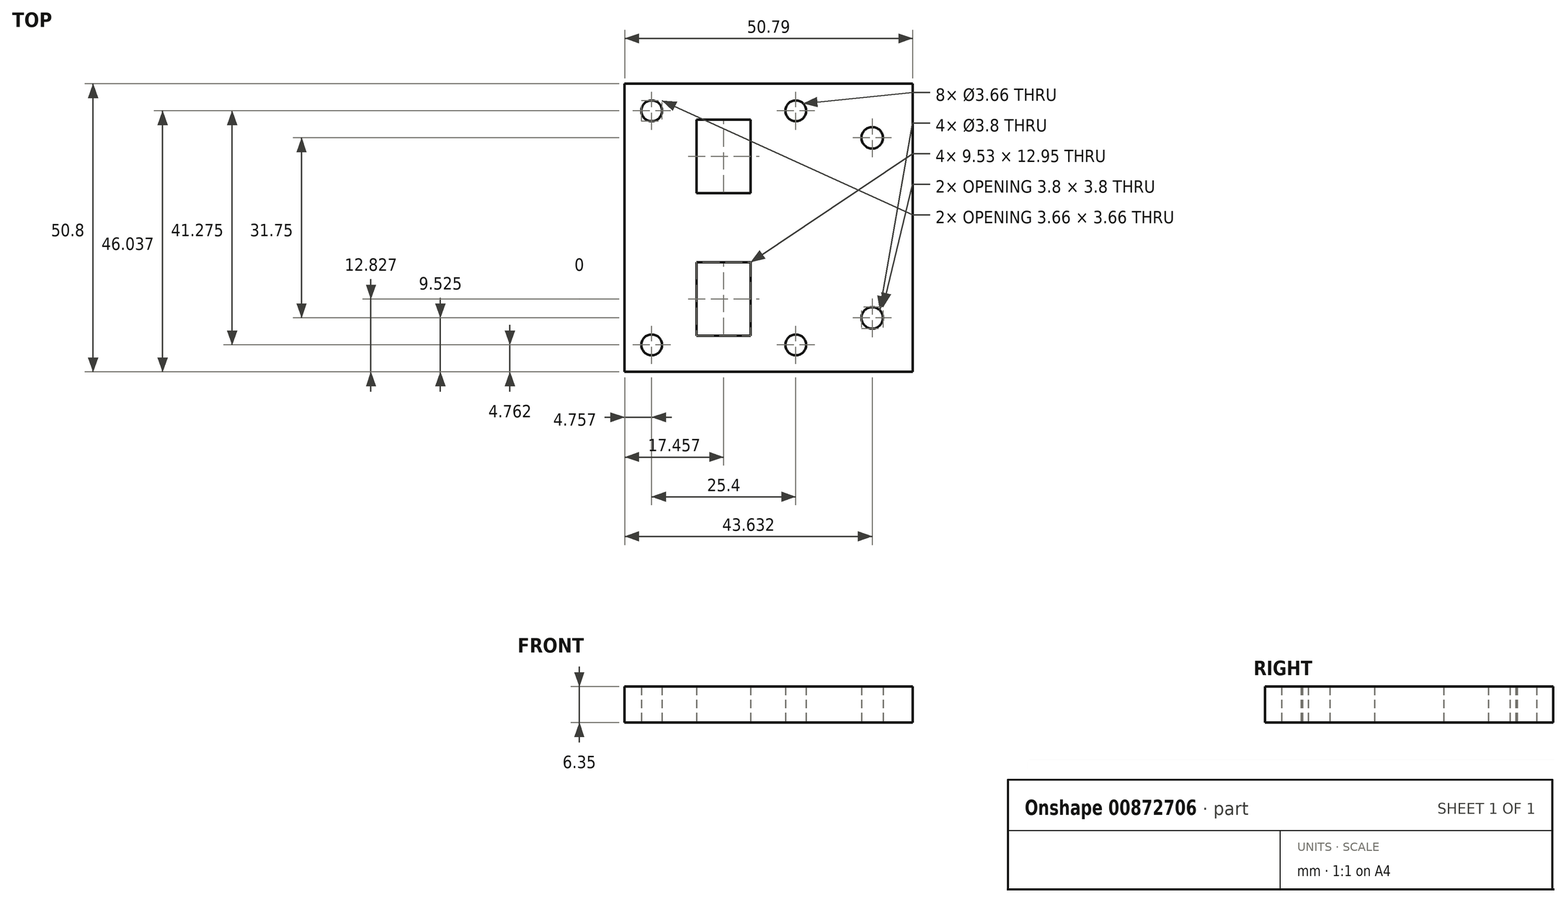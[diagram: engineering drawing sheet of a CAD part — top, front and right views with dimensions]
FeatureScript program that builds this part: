
annotation { "Feature Type Name" : "Feature", "Feature Type Description" : "" }
export const myFeature = defineFeature(function(context is Context, id is Id, definition is map)
    precondition{}
    {
        {
            var Q0;
            Q0=qCreatedBy(makeId("Top.planeOp"),FACE);
            var sketch = newSketch(context, id + "F0", { "sketchPlane" : qUnion([Q0])});
            skLineSegment(sketch, "E0.bottom", {"start": v(-152.4, 152.4) * mm, "end": v(152.4, 152.4) * mm});
            skLineSegment(sketch, "E0.top", {"start": v(-152.4, -152.4) * mm, "end": v(152.4, -152.4) * mm});
            skLineSegment(sketch, "E0.left", {"start": v(-152.4, 152.4) * mm, "end": v(-152.4, -152.4) * mm});
            skLineSegment(sketch, "E0.right", {"start": v(152.4, 152.4) * mm, "end": v(152.4, -152.4) * mm});
            skPoint(sketch, "E0.middle", {"position": v(0, 0) * mm});
            skLineSegment(sketch, "E1.0", {"start": v(-107.95, -82.55) * mm, "end": v(107.95, -82.55) * mm});
            skLineSegment(sketch, "E2.0", {"start": v(-107.95, 107.95) * mm, "end": v(-107.95, -82.55) * mm});
            skLineSegment(sketch, "E3", {"start": v(0, 152.4) * mm, "end": v(0, -152.4) * mm, "construction": true});
            skLineSegment(sketch, "E4", {"start": v(-152.4, 0) * mm, "end": v(152.4, 0) * mm, "construction": true});
            skLineSegment(sketch, "E5.MirrorCS", {"start": v(107.95, 107.95) * mm, "end": v(107.95, -82.55) * mm});
            skLineSegment(sketch, "E6.0", {"start": v(-107.95, 107.95) * mm, "end": v(107.95, 107.95) * mm});
            skLineSegment(sketch, "E7.bottom", {"start": v(-104.78, 25.4) * mm, "end": v(-53.98, 25.4) * mm});
            skLineSegment(sketch, "E7.top", {"start": v(-104.78, -25.4) * mm, "end": v(-53.98, -25.4) * mm});
            skLineSegment(sketch, "E7.left", {"start": v(-104.78, 25.4) * mm, "end": v(-104.78, -25.4) * mm});
            skLineSegment(sketch, "E7.right", {"start": v(-69.85, 25.4) * mm, "end": v(-69.85, -25.4) * mm});
            skLineSegment(sketch, "E8", {"start": v(-87.31, 25.4) * mm, "end": v(-87.31, -152.4) * mm, "construction": true});
            skLineSegment(sketch, "E9.bottom", {"start": v(-82.55, 6.1) * mm, "end": v(-92.08, 6.1) * mm});
            skLineSegment(sketch, "E9.top", {"start": v(-82.55, 19.05) * mm, "end": v(-92.08, 19.05) * mm});
            skLineSegment(sketch, "E9.left", {"start": v(-82.55, 6.1) * mm, "end": v(-82.55, 19.05) * mm});
            skLineSegment(sketch, "E9.right", {"start": v(-92.08, 6.1) * mm, "end": v(-92.08, 19.05) * mm});
            skPoint(sketch, "E9.middle", {"position": v(-87.31, 12.57) * mm});
            skPoint(sketch, "E10", {"position": v(-69.85, 0) * mm});
            skLineSegment(sketch, "E11.MirrorCS", {"start": v(-92.08, -6.1) * mm, "end": v(-92.08, -19.05) * mm});
            skLineSegment(sketch, "E12.MirrorCS", {"start": v(-82.55, -6.1) * mm, "end": v(-82.55, -19.05) * mm});
            skPoint(sketch, "E13.MirrorP", {"position": v(-87.31, -12.57) * mm});
            skLineSegment(sketch, "E14.MirrorCS", {"start": v(-82.55, -6.1) * mm, "end": v(-92.08, -6.1) * mm});
            skLineSegment(sketch, "E15.MirrorCS", {"start": v(-82.55, -19.05) * mm, "end": v(-92.08, -19.05) * mm});
            skCircle(sketch, "E16", {"center": v(-101.6, -127) * mm, "radius": 11.43 * mm});
            skCircle(sketch, "E17", {"center": v(-86.1, -111.5) * mm, "radius": 1.59 * mm});
            skCircle(sketch, "E18.1.0", {"center": v(-117.1, -111.5) * mm, "radius": 1.59 * mm});
            skCircle(sketch, "E18.2.0", {"center": v(-117.1, -142.5) * mm, "radius": 1.59 * mm});
            skCircle(sketch, "E18.3.0", {"center": v(-86.1, -142.5) * mm, "radius": 1.59 * mm});
            skCircle(sketch, "E19.MirrorC", {"center": v(117.1, -111.5) * mm, "radius": 1.59 * mm});
            skCircle(sketch, "E20.MirrorC", {"center": v(86.1, -111.5) * mm, "radius": 1.59 * mm});
            skCircle(sketch, "E21.MirrorC", {"center": v(117.1, -142.5) * mm, "radius": 1.59 * mm});
            skPoint(sketch, "E22.MirrorP", {"position": v(101.6, -127) * mm});
            skCircle(sketch, "E23.MirrorC", {"center": v(86.1, -142.5) * mm, "radius": 1.59 * mm});
            skCircle(sketch, "E24.MirrorC", {"center": v(101.6, -127) * mm, "radius": 11.43 * mm});
            skPoint(sketch, "E25.orphan", {"position": v(-87.31, -25.4) * mm});
            skCircle(sketch, "E26", {"center": v(-103.19, -89.7) * mm, "radius": 1.59 * mm});
            skCircle(sketch, "E27.MirrorC", {"center": v(-71.44, -89.7) * mm, "radius": 1.59 * mm});
            skLineSegment(sketch, "E28.bottom", {"start": v(-96.84, -82.55) * mm, "end": v(-77.79, -82.55) * mm});
            skLineSegment(sketch, "E28.top", {"start": v(-96.84, -96.85) * mm, "end": v(-77.79, -96.85) * mm});
            skLineSegment(sketch, "E28.left", {"start": v(-96.84, -82.55) * mm, "end": v(-96.84, -96.85) * mm});
            skLineSegment(sketch, "E28.right", {"start": v(-77.79, -82.55) * mm, "end": v(-77.79, -96.85) * mm});
            skPoint(sketch, "E29", {"position": v(-87.31, -96.85) * mm});
            skLineSegment(sketch, "E30.MirrorCS", {"start": v(96.84, -82.55) * mm, "end": v(96.84, -96.85) * mm});
            skCircle(sketch, "E31.MirrorC", {"center": v(71.44, -89.7) * mm, "radius": 1.59 * mm});
            skCircle(sketch, "E32.MirrorC", {"center": v(103.19, -89.7) * mm, "radius": 1.59 * mm});
            skLineSegment(sketch, "E33.MirrorCS", {"start": v(96.84, -82.55) * mm, "end": v(77.79, -82.55) * mm});
            skPoint(sketch, "E34.MirrorP", {"position": v(87.31, -96.85) * mm});
            skLineSegment(sketch, "E35.MirrorCS", {"start": v(77.79, -82.55) * mm, "end": v(77.79, -96.85) * mm});
            skLineSegment(sketch, "E36.MirrorCS", {"start": v(96.84, -96.85) * mm, "end": v(77.79, -96.85) * mm});
            skLineSegment(sketch, "E37", {"start": v(107.95, 12.7) * mm, "end": v(-107.95, 12.57) * mm, "construction": true});
            skCircle(sketch, "E38.MirrorC", {"center": v(-103.3, 114.85) * mm, "radius": 1.59 * mm});
            skLineSegment(sketch, "E39.MirrorCS", {"start": v(-96.97, 122) * mm, "end": v(-77.92, 122.03) * mm});
            skLineSegment(sketch, "E40.MirrorCS", {"start": v(-96.95, 107.7) * mm, "end": v(-77.9, 107.73) * mm});
            skCircle(sketch, "E41.MirrorC", {"center": v(103.07, 115.1) * mm, "radius": 1.59 * mm});
            skLineSegment(sketch, "E42.MirrorCS", {"start": v(-96.95, 107.7) * mm, "end": v(-96.97, 122) * mm});
            skCircle(sketch, "E43.MirrorC", {"center": v(-71.56, 114.89) * mm, "radius": 1.59 * mm});
            skLineSegment(sketch, "E44.MirrorCS", {"start": v(96.7, 122.24) * mm, "end": v(77.66, 122.21) * mm});
            skCircle(sketch, "E45.MirrorC", {"center": v(71.32, 115.06) * mm, "radius": 1.59 * mm});
            skLineSegment(sketch, "E46.MirrorCS", {"start": v(96.73, 107.94) * mm, "end": v(77.68, 107.91) * mm});
            skPoint(sketch, "E47.MirrorP", {"position": v(-87.44, 122.02) * mm});
            skPoint(sketch, "E48.MirrorP", {"position": v(87.18, 122.23) * mm});
            skLineSegment(sketch, "E49.MirrorCS", {"start": v(-108.06, 107.7) * mm, "end": v(107.84, 107.95) * mm});
            skLineSegment(sketch, "E50.MirrorCS", {"start": v(77.68, 107.91) * mm, "end": v(77.66, 122.21) * mm});
            skLineSegment(sketch, "E51.MirrorCS", {"start": v(-77.9, 107.73) * mm, "end": v(-77.92, 122.03) * mm});
            skLineSegment(sketch, "E52.MirrorCS", {"start": v(96.73, 107.94) * mm, "end": v(96.7, 122.24) * mm});
            skLineSegment(sketch, "E53.0", {"start": v(-53.98, 25.4) * mm, "end": v(-53.98, -25.4) * mm});
            skCircle(sketch, "E54", {"center": v(-61.14, 15.87) * mm, "radius": 1.59 * mm});
            skCircle(sketch, "E55.MirrorC", {"center": v(-61.14, -15.88) * mm, "radius": 1.59 * mm});
            skCircle(sketch, "E56", {"center": v(-100.01, 20.64) * mm, "radius": 1.83 * mm});
            skCircle(sketch, "E57.MirrorC", {"center": v(-100.01, -20.64) * mm, "radius": 1.83 * mm});
            skCircle(sketch, "E58.MirrorC", {"center": v(-74.61, 20.64) * mm, "radius": 1.83 * mm});
            skCircle(sketch, "E59.MirrorC", {"center": v(-74.61, -20.64) * mm, "radius": 1.83 * mm});
            skSolve(sketch);
        }
        {
            var Q0;
            {var subQ1=sQuery(id+"F0.wireOp",EDGE,"E7.right");Q0=makeQuery(id+"F0.imprint","IMPRINT",FACE,{"disambiguationData":[TD([[makeQuery(id+"F0.imprint","IMPRINT",EDGE,{"derivedFrom":subQ1}),1.0]])]});}
            var Q1;
            {var subQ0=sQuery(id+"F0.wireOp",EDGE,"E7.left");Q1=makeQuery(id+"F0.imprint","IMPRINT",FACE,{"disambiguationData":[TD([[makeQuery(id+"F0.imprint","IMPRINT",EDGE,{"derivedFrom":subQ0}),1.0]])]});}
            var Q2;
            Q2=makeQuery(id+"F0.imprint","IMPRINT",FACE,{"disambiguationData":[TD([[makeQuery(id+"F0.imprint","IMPRINT",EDGE,{"derivedFrom":sQuery(id+"F0.wireOp",EDGE,"E57.MirrorC")}),-1.0]])]});
            var Q3;
            Q3=makeQuery(id+"F0.imprint","IMPRINT",FACE,{"disambiguationData":[TD([[makeQuery(id+"F0.imprint","IMPRINT",EDGE,{"derivedFrom":sQuery(id+"F0.wireOp",EDGE,"E56")}),1.0]])]});
            var Q4;
            Q4=makeQuery(id+"F0.imprint","IMPRINT",FACE,{"disambiguationData":[TD([[makeQuery(id+"F0.imprint","IMPRINT",EDGE,{"derivedFrom":sQuery(id+"F0.wireOp",EDGE,"E58.MirrorC")}),-1.0]])]});
            var Q5;
            Q5=makeQuery(id+"F0.imprint","IMPRINT",FACE,{"disambiguationData":[TD([[makeQuery(id+"F0.imprint","IMPRINT",EDGE,{"derivedFrom":sQuery(id+"F0.wireOp",EDGE,"E59.MirrorC")}),1.0]])]});
            var Q6;
            Q6=makeQuery(id+"F0.imprint","IMPRINT",FACE,{"disambiguationData":[TD([[makeQuery(id+"F0.imprint","IMPRINT",EDGE,{"derivedFrom":sQuery(id+"F0.wireOp",EDGE,"E54")}),1.0]])]});
            var Q7;
            Q7=makeQuery(id+"F0.imprint","IMPRINT",FACE,{"disambiguationData":[TD([[makeQuery(id+"F0.imprint","IMPRINT",EDGE,{"derivedFrom":sQuery(id+"F0.wireOp",EDGE,"E55.MirrorC")}),-1.0]])]});
            var Q8;
            {var subQ3=sQuery(id+"F0.wireOp",EDGE,"E7.right");Q8=makeQuery(id+"F0.imprint","IMPRINT",FACE,{"disambiguationData":[TD([[makeQuery(id+"F0.imprint","IMPRINT",EDGE,{"derivedFrom":subQ3}),-1.0]])]});}
            extrude(context, id + "F1", {"entities" : qUnion([Q0, Q1, Q2, Q3, Q4, Q5, Q6, Q7, Q8]), "depth" : 6.35 * mm, "offsetDistance" : 25.4 * mm});
        }
        {
            var Q0;
            Q0=sQuery(id+"F0.wireOp",VERTEX,"E56.center");
            var Q1;
            Q1=sQuery(id+"F0.wireOp",VERTEX,"E58.MirrorC.center");
            var Q2;
            Q2=sQuery(id+"F0.wireOp",VERTEX,"E59.MirrorC.center");
            var Q3;
            Q3=sQuery(id+"F0.wireOp",VERTEX,"E57.MirrorC.center");
            var Q4;
            Q4=makeQuery(id+"F1.opExtrude","SWEPT_BODY",BODY,{"disambiguationData":[OSD([sQuery(id+"F0.wireOp",EDGE,"E7.bottom"),sQuery(id+"F0.wireOp",EDGE,"E7.top"),sQuery(id+"F0.wireOp",EDGE,"E7.left"),sQuery(id+"F0.wireOp",EDGE,"E9.bottom"),sQuery(id+"F0.wireOp",EDGE,"E9.top"),sQuery(id+"F0.wireOp",EDGE,"E9.left"),sQuery(id+"F0.wireOp",EDGE,"E9.right"),sQuery(id+"F0.wireOp",EDGE,"E11.MirrorCS"),sQuery(id+"F0.wireOp",EDGE,"E12.MirrorCS"),sQuery(id+"F0.wireOp",EDGE,"E14.MirrorCS"),sQuery(id+"F0.wireOp",EDGE,"E15.MirrorCS"),sQuery(id+"F0.wireOp",EDGE,"E53.0")])]});
            hole(context, id + "F2", {"style" : HoleStyle.SIMPLE, "endStyle" : HoleEndStyle.THROUGH, "oppositeDirection" : true, "standardTappedOrClearance" : lookupTablePath({ "fit" : "Close", "standard" : "ANSI", "size" : "#6", "type" : "Clearance" }), "standardBlindInLast" : lookupTablePath({ "fit" : "Close", "standard" : "ANSI", "size" : "#6", "type" : "Clearance" }), "holeDiameter" : 3.66 * mm, "majorDiameter" : 6.35 * mm, "isTappedThrough" : true, "tappedDepth" : 12.7 * mm, "tapClearance" : 3, "locations" : qUnion([Q0, Q1, Q2, Q3]), "scope" : qUnion([Q4])});
        }
        {
            var Q0;
            Q0=sQuery(id+"F0.wireOp",VERTEX,"E55.MirrorC.center");
            var Q1;
            Q1=sQuery(id+"F0.wireOp",VERTEX,"E54.center");
            var Q2;
            Q2=makeQuery(id+"F1.opExtrude","SWEPT_BODY",BODY,{"disambiguationData":[OSD([sQuery(id+"F0.wireOp",EDGE,"E7.bottom"),sQuery(id+"F0.wireOp",EDGE,"E7.top"),sQuery(id+"F0.wireOp",EDGE,"E7.left"),sQuery(id+"F0.wireOp",EDGE,"E9.bottom"),sQuery(id+"F0.wireOp",EDGE,"E9.top"),sQuery(id+"F0.wireOp",EDGE,"E9.left"),sQuery(id+"F0.wireOp",EDGE,"E9.right"),sQuery(id+"F0.wireOp",EDGE,"E11.MirrorCS"),sQuery(id+"F0.wireOp",EDGE,"E12.MirrorCS"),sQuery(id+"F0.wireOp",EDGE,"E14.MirrorCS"),sQuery(id+"F0.wireOp",EDGE,"E15.MirrorCS"),sQuery(id+"F0.wireOp",EDGE,"E53.0")])]});
            hole(context, id + "F3", {"style" : HoleStyle.SIMPLE, "endStyle" : HoleEndStyle.THROUGH, "oppositeDirection" : true, "standardTappedOrClearance" : lookupTablePath({ "fit" : "Normal (ASME)", "standard" : "ANSI", "size" : "#6", "type" : "Clearance" }), "standardBlindInLast" : lookupTablePath({ "fit" : "Free", "standard" : "ANSI", "size" : "#6", "type" : "Clearance" }), "holeDiameter" : 3.8 * mm, "majorDiameter" : 3.5 * mm, "isTappedThrough" : true, "tappedDepth" : 12.7 * mm, "tapClearance" : 3, "locations" : qUnion([Q0, Q1]), "scope" : qUnion([Q2])});
        }
    });
